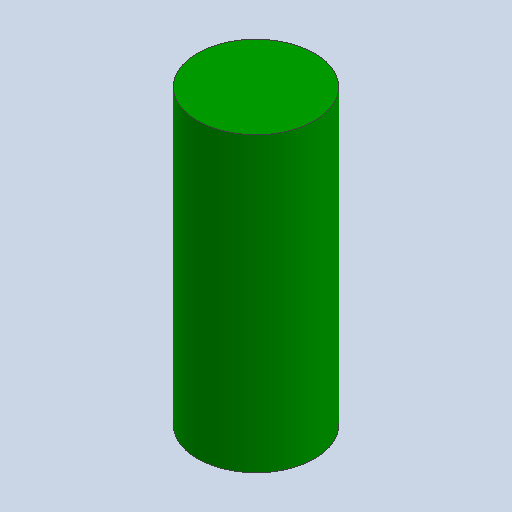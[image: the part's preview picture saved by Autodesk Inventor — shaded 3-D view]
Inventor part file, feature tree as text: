
AUTODESK INVENTOR PART (.ipt)
format: ipt  version: 2025.2 (Build 292293000, 293)  size: 89,600 bytes
history: native  units: in
note: dims shown in document units (in); Inventor stores cm internally (conversion verified against a paired STEP export)
features: other x3, sketch x1
ambient origin geometry x8: Origin, YZ Plane, XZ Plane, XY Plane, X Axis, Y Axis, Z Axis, Center Point
bodies: Solid1 (feature_tree)
feature tree (4):
  other  "26650(Green).ipt"
  other  "Solid1::26650(Green).ipt"
  other  "TaggingFeature1"
  sketch  "Sketch1"  dims[d0=0.3937in]
